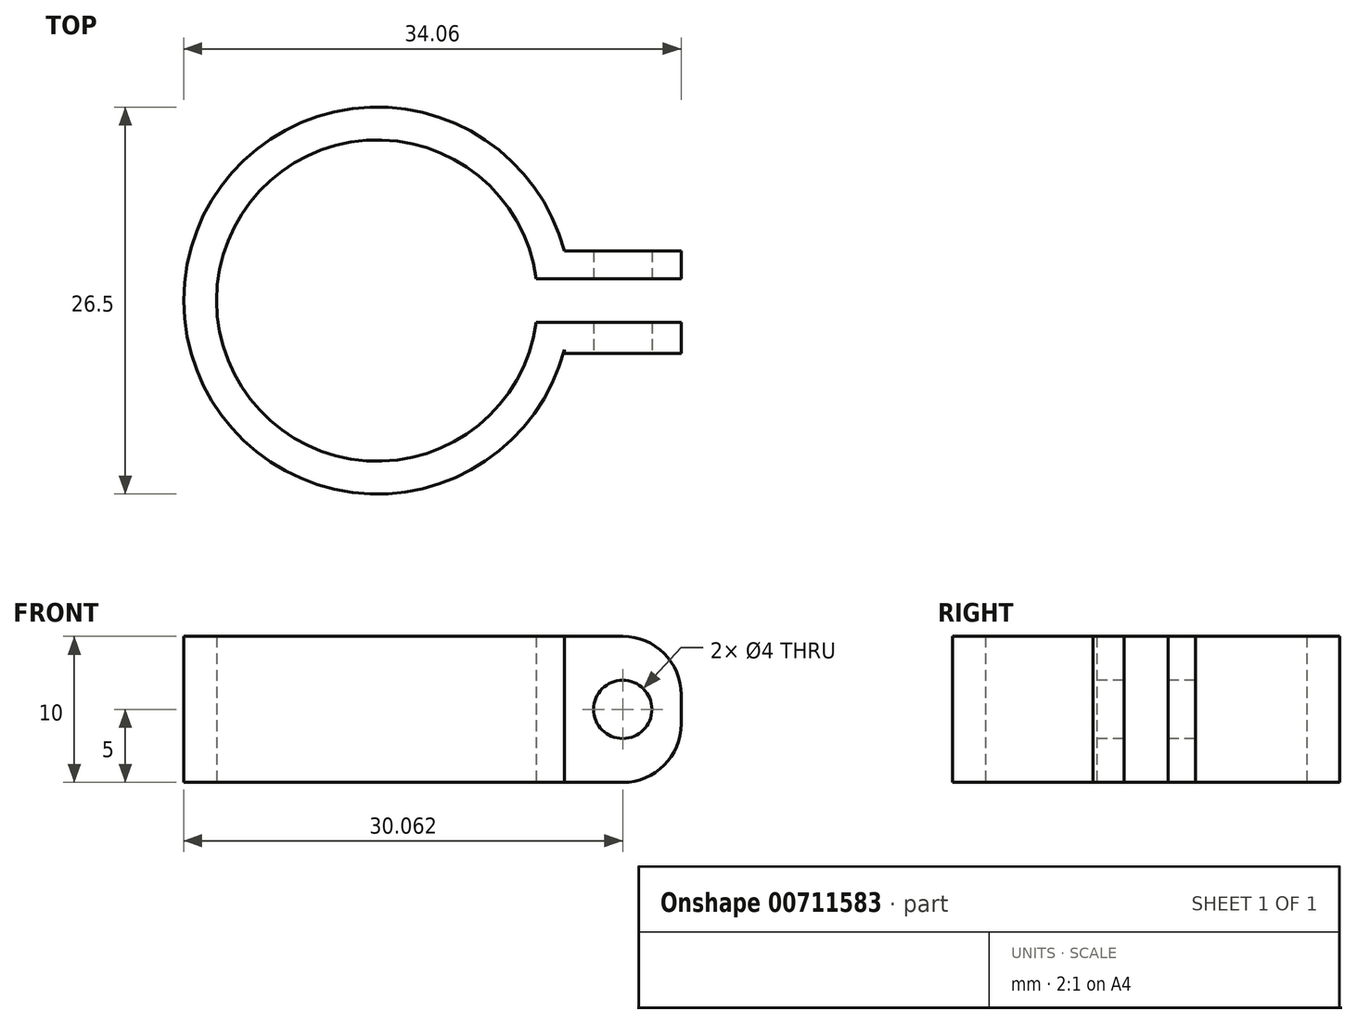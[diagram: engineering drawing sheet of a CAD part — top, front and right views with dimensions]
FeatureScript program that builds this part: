
annotation { "Feature Type Name" : "Feature", "Feature Type Description" : "" }
export const myFeature = defineFeature(function(context is Context, id is Id, definition is map)
    precondition{}
    {
        {
            var Q0;
            Q0=qCreatedBy(makeId("Top.planeOp"),FACE);
            var sketch = newSketch(context, id + "F0", { "sketchPlane" : qUnion([Q0])});
            skCircle(sketch, "E0", {"center": v(0, 0) * mm, "radius": 11 * mm});
            skArc(sketch, "E1", {"start": v(12.81, 3.38) * mm, "mid": v(-13.25, 0) * mm, "end": v(12.81, -3.38) * mm});
            skLineSegment(sketch, "E2.bottom", {"start": v(12.81, 3.38) * mm, "end": v(20.81, 3.38) * mm});
            skLineSegment(sketch, "E2.top", {"start": v(12.81, -3.62) * mm, "end": v(20.81, -3.62) * mm});
            skLineSegment(sketch, "E2.right", {"start": v(20.81, 3.38) * mm, "end": v(20.81, -3.62) * mm});
            skLineSegment(sketch, "E3", {"start": v(20.81, 0) * mm, "end": v(0, 0) * mm, "construction": true});
            skLineSegment(sketch, "E4.trimOffspring", {"start": v(12.81, -3.38) * mm, "end": v(12.81, -3.62) * mm});
            skSolve(sketch);
        }
        {
            var Q0;
            Q0=makeQuery(id+"F0.imprint","IMPRINT",FACE,{"disambiguationData":[TD([[makeQuery(id+"F0.imprint","IMPRINT",EDGE,{"derivedFrom":sQuery(id+"F0.wireOp",EDGE,"cHZqtPlu-NH5j-nOJe-kCKd-jvIIEfFLhisE")}),1.0]])]});
            var Q1;
            Q1=makeQuery(id+"F0.imprint","IMPRINT",FACE,{"disambiguationData":[TD([[makeQuery(id+"F0.imprint","IMPRINT",EDGE,{"derivedFrom":sQuery(id+"F0.wireOp",EDGE,"E0")}),-1.0]])]});
            var Q2;
            {var subQ4=sQuery(id+"F0.wireOp",EDGE,"E2.bottom");Q2=makeQuery(id+"F0.imprint","IMPRINT",FACE,{"disambiguationData":[TD([[makeQuery(id+"F0.imprint","IMPRINT",EDGE,{"derivedFrom":subQ4}),-1.0]])]});}
            extrude(context, id + "F1", {"entities" : qUnion([Q0, Q1, Q2]), "depth" : 10 * mm, "offsetDistance" : 25 * mm});
        }
        {
            var Q0;
            Q0=qCreatedBy(makeId("Top.planeOp"),FACE);
            var sketch = newSketch(context, id + "F2", { "sketchPlane" : qUnion([Q0])});
            skLineSegment(sketch, "E5.bottom", {"start": v(5.87, -1.5) * mm, "end": v(32.65, -1.5) * mm});
            skLineSegment(sketch, "E5.top", {"start": v(5.87, 1.5) * mm, "end": v(32.65, 1.5) * mm});
            skLineSegment(sketch, "E5.left", {"start": v(5.87, -1.5) * mm, "end": v(5.87, 1.5) * mm});
            skLineSegment(sketch, "E5.right", {"start": v(32.65, -1.5) * mm, "end": v(32.65, 1.5) * mm});
            skLineSegment(sketch, "E6", {"start": v(5.87, 0) * mm, "end": v(0, 0) * mm, "construction": true});
            skSolve(sketch);
        }
        {
            var Q0;
            Q0=makeQuery(id+"F2.imprint","IMPRINT",FACE,{"disambiguationData":[TD([[makeQuery(id+"F2.imprint","IMPRINT",EDGE,{"derivedFrom":sQuery(id+"F2.wireOp",EDGE,"E5.bottom")}),1.0]])]});
            var Q1;
            Q1=makeQuery(id+"F1.opExtrude","CAP_FACE",FACE,{"disambiguationData":[OSD([sQuery(id+"F0.wireOp",EDGE,"E0"),sQuery(id+"F0.wireOp",EDGE,"E1"),sQuery(id+"F0.wireOp",EDGE,"E2.bottom"),sQuery(id+"F0.wireOp",EDGE,"E2.top"),sQuery(id+"F0.wireOp",EDGE,"E2.right"),sQuery(id+"F0.wireOp",EDGE,"E4.trimOffspring")])],"isStart":false});
            extrude(context, id + "F3", {"entities" : qUnion([Q0]), "operationType" : NewBodyOperationType.REMOVE, "endBound" : BoundingType.SYMMETRIC, "depth" : 23 * mm, "endBoundEntityFace" : qUnion([Q1]), "offsetDistance" : 25 * mm});
        }
        {
            var Q0;
            Q0=makeQuery(id+"F1.opExtrude","SWEPT_FACE",FACE,{"disambiguationData":[OSD([sQuery(id+"F0.wireOp",EDGE,"E2.top")])]});
            var sketch = newSketch(context, id + "F4", { "sketchPlane" : qUnion([Q0])});
            skCircle(sketch, "E7", {"center": v(16.81, 5) * mm, "radius": 2 * mm});
            skPoint(sketch, "E7.centerSnap0", {"position": v(16.81, 10) * mm});
            skPoint(sketch, "E7.centerSnap1", {"position": v(12.81, 5) * mm});
            skSolve(sketch);
        }
        {
            var Q0;
            Q0=makeQuery(id+"F4.imprint","IMPRINT",FACE,{"disambiguationData":[TD([[makeQuery(id+"F4.imprint","IMPRINT",EDGE,{"derivedFrom":sQuery(id+"F4.wireOp",EDGE,"E7")}),1.0]])]});
            extrude(context, id + "F5", {"entities" : qUnion([Q0]), "operationType" : NewBodyOperationType.REMOVE, "oppositeDirection" : true, "depth" : 25 * mm, "offsetDistance" : 25 * mm});
        }
        {
            var Q0;
            {var subQ0=sQuery(id+"F0.wireOp",EDGE,"E2.right");var subQ1=sQuery(id+"F0.wireOp",EDGE,"E2.top");Q0=makeQuery(id+"F3.boolean.opBoolean","SPLIT",EDGE,{"disambiguationData":[TD([makeQuery(id+"F1.opExtrude","SWEPT_FACE",FACE,{"disambiguationData":[OSD([subQ1])]})])],"derivedFrom":makeQuery(id+"F1.opExtrude","CAP_EDGE",EDGE,{"disambiguationData":[OSD([subQ0])],"isStart":false})});}
            var Q1;
            {var subQ0=sQuery(id+"F0.wireOp",EDGE,"E2.right");var subQ1=sQuery(id+"F0.wireOp",EDGE,"E2.bottom");Q1=makeQuery(id+"F3.boolean.opBoolean","SPLIT",EDGE,{"disambiguationData":[TD([makeQuery(id+"F1.opExtrude","SWEPT_FACE",FACE,{"disambiguationData":[OSD([subQ1])]})])],"derivedFrom":makeQuery(id+"F1.opExtrude","CAP_EDGE",EDGE,{"disambiguationData":[OSD([subQ0])],"isStart":false})});}
            var Q2;
            {var subQ0=sQuery(id+"F0.wireOp",EDGE,"E2.right");var subQ1=sQuery(id+"F0.wireOp",EDGE,"E2.bottom");Q2=makeQuery(id+"F3.boolean.opBoolean","SPLIT",EDGE,{"disambiguationData":[TD([makeQuery(id+"F1.opExtrude","SWEPT_FACE",FACE,{"disambiguationData":[OSD([subQ1])]})])],"derivedFrom":makeQuery(id+"F1.opExtrude","CAP_EDGE",EDGE,{"disambiguationData":[OSD([subQ0])],"isStart":true})});}
            var Q3;
            {var subQ0=sQuery(id+"F0.wireOp",EDGE,"E2.right");var subQ1=sQuery(id+"F0.wireOp",EDGE,"E2.top");Q3=makeQuery(id+"F3.boolean.opBoolean","SPLIT",EDGE,{"disambiguationData":[TD([makeQuery(id+"F1.opExtrude","SWEPT_FACE",FACE,{"disambiguationData":[OSD([subQ1])]})])],"derivedFrom":makeQuery(id+"F1.opExtrude","CAP_EDGE",EDGE,{"disambiguationData":[OSD([subQ0])],"isStart":true})});}
            fillet(context, id + "F6", {"entities" : qUnion([Q0, Q1, Q2, Q3]), "radius" : 4 * mm, "tangentPropagation" : true, "allowEdgeOverflow" : false});
        }
    });
